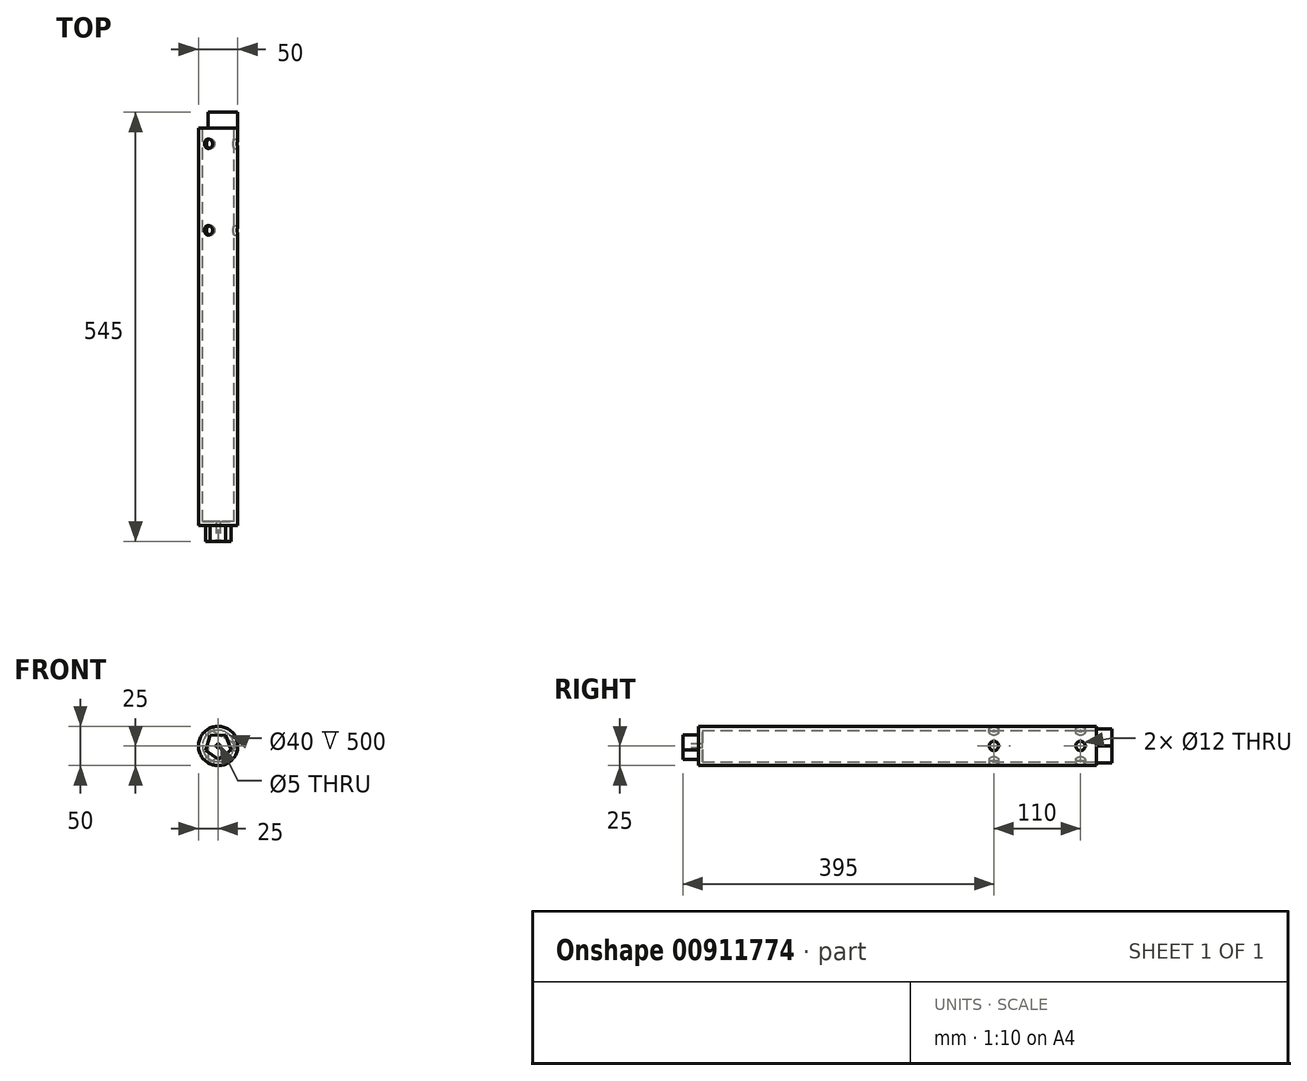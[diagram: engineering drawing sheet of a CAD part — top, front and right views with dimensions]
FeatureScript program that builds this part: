
annotation { "Feature Type Name" : "Feature", "Feature Type Description" : "" }
export const myFeature = defineFeature(function(context is Context, id is Id, definition is map)
    precondition{}
    {
        {
            var Q0;
            Q0=qCreatedBy(makeId("Front.planeOp"),FACE);
            var sketch = newSketch(context, id + "F0", { "sketchPlane" : qUnion([Q0])});
            skCircle(sketch, "E0", {"center": v(0, 0) * mm, "radius": 25 * mm});
            skCircle(sketch, "E1", {"center": v(0, 0) * mm, "radius": 20 * mm});
            skSolve(sketch);
        }
        {
            var Q0;
            Q0=makeQuery(id+"F0.imprint","IMPRINT",FACE,{"disambiguationData":[TD([[makeQuery(id+"F0.imprint","IMPRINT",EDGE,{"derivedFrom":sQuery(id+"F0.wireOp",EDGE,"E0")}),1.0]])]});
            extrude(context, id + "F1", {"entities" : qUnion([Q0]), "depth" : 500 * mm, "offsetDistance" : 25 * mm});
        }
        {
            var Q0;
            Q0=makeQuery(id+"F1.opExtrude","CAP_FACE",FACE,{"disambiguationData":[OSD([sQuery(id+"F0.wireOp",EDGE,"E0"),sQuery(id+"F0.wireOp",EDGE,"E1")])],"isStart":false});
            var sketch = newSketch(context, id + "F2", { "sketchPlane" : qUnion([Q0])});
            skCircle(sketch, "E2", {"center": v(0, 0) * mm, "radius": 25 * mm});
            skSolve(sketch);
        }
        {
            var Q0;
            Q0=qSketchRegion(id+"F2",true);
            extrude(context, id + "F3", {"entities" : qUnion([Q0]), "operationType" : NewBodyOperationType.ADD, "depth" : 5 * mm, "offsetDistance" : 25 * mm});
        }
        {
            var Q0;
            Q0=makeQuery(id+"F3.opExtrude","CAP_FACE",FACE,{"disambiguationData":[OSD([sQuery(id+"F2.wireOp",EDGE,"E2")])],"isStart":false});
            var sketch = newSketch(context, id + "F4", { "sketchPlane" : qUnion([Q0])});
            skCircle(sketch, "E3.cCircle", {"center": v(0, 0) * mm, "radius": 13.77 * mm, "construction": true});
            skLineSegment(sketch, "E3.0", {"start": v(0.38, -17.01) * mm, "end": v(-16.06, -5.62) * mm});
            skLineSegment(sketch, "E3.1", {"start": v(-16.06, -5.62) * mm, "end": v(-10.3, 13.54) * mm});
            skLineSegment(sketch, "E3.2", {"start": v(-10.3, 13.54) * mm, "end": v(9.7, 13.99) * mm});
            skLineSegment(sketch, "E3.3", {"start": v(9.7, 13.99) * mm, "end": v(16.3, -4.9) * mm});
            skLineSegment(sketch, "E3.4", {"start": v(16.3, -4.9) * mm, "end": v(0.38, -17.01) * mm});
            skPoint(sketch, "E3.0.midPoint", {"position": v(-7.84, -11.32) * mm});
            skSolve(sketch);
        }
        {
            var Q0;
            Q0=makeQuery(id+"F4.imprint","IMPRINT",FACE,{"disambiguationData":[TD([[makeQuery(id+"F4.imprint","IMPRINT",EDGE,{"derivedFrom":sQuery(id+"F4.wireOp",EDGE,"E3.0")}),-1.0]])]});
            extrude(context, id + "F5", {"entities" : qUnion([Q0]), "operationType" : NewBodyOperationType.ADD, "depth" : 20 * mm, "offsetDistance" : 25 * mm});
        }
        {
            var Q0;
            Q0=makeQuery(id+"F5.opExtrude","CAP_FACE",FACE,{"disambiguationData":[OSD([sQuery(id+"F4.wireOp",EDGE,"E3.0"),sQuery(id+"F4.wireOp",EDGE,"E3.1"),sQuery(id+"F4.wireOp",EDGE,"E3.2"),sQuery(id+"F4.wireOp",EDGE,"E3.3"),sQuery(id+"F4.wireOp",EDGE,"E3.4")])],"isStart":false});
            var sketch = newSketch(context, id + "F6", { "sketchPlane" : qUnion([Q0])});
            skPoint(sketch, "E4", {"position": v(0, 0) * mm});
            skSolve(sketch);
        }
        {
            var Q0;
            Q0=sQuery(id+"F6.wireOp",VERTEX,"E4");
            var Q1;
            Q1=makeQuery(id+"F1.opExtrude","SWEPT_BODY",BODY,{"disambiguationData":[OSD([sQuery(id+"F0.wireOp",EDGE,"E0"),sQuery(id+"F0.wireOp",EDGE,"E1")])]});
            hole(context, id + "F7", {"style" : HoleStyle.SIMPLE, "endStyle" : HoleEndStyle.THROUGH, "holeDiameter" : 5 * mm, "majorDiameter" : 5 * mm, "isTappedThrough" : true, "tappedDepth" : 12 * mm, "tapClearance" : 3, "locations" : qUnion([Q0]), "scope" : qUnion([Q1])});
        }
        {
            var Q0;
            Q0=qCreatedBy(makeId("Right.planeOp"),FACE);
            cPlane(context, id + "F8", {"entities" : qUnion([Q0]), "cplaneType" : CPlaneType.OFFSET, "offset" : 25 * mm, "width" : 150 * mm, "height" : 150 * mm});
        }
        {
            var Q0;
            Q0=qCreatedBy(id+"F8.planeOp",FACE);
            var sketch = newSketch(context, id + "F9", { "sketchPlane" : qUnion([Q0])});
            skPoint(sketch, "E5", {"position": v(-20, 0) * mm});
            skPoint(sketch, "E6", {"position": v(-130, 0) * mm});
            skSolve(sketch);
        }
        {
            var Q0;
            Q0=sQuery(id+"F9.wireOp",VERTEX,"E5");
            var Q1;
            Q1=sQuery(id+"F9.wireOp",VERTEX,"E6");
            var Q2;
            Q2=makeQuery(id+"F1.opExtrude","SWEPT_BODY",BODY,{"disambiguationData":[OSD([sQuery(id+"F0.wireOp",EDGE,"E0"),sQuery(id+"F0.wireOp",EDGE,"E1")])]});
            hole(context, id + "F10", {"style" : HoleStyle.SIMPLE, "endStyle" : HoleEndStyle.BLIND, "holeDiameter" : 12 * mm, "majorDiameter" : 5 * mm, "holeDepth" : 6 * mm, "isTappedThrough" : true, "tappedDepth" : 12 * mm, "tapClearance" : 3, "locations" : qUnion([Q0, Q1]), "scope" : qUnion([Q2])});
        }
        {
            var Q0;
            Q0=makeQuery(id+"F1.opExtrude","CAP_FACE",FACE,{"disambiguationData":[OSD([sQuery(id+"F0.wireOp",EDGE,"E0"),sQuery(id+"F0.wireOp",EDGE,"E1")])],"isStart":true});
            var sketch = newSketch(context, id + "F11", { "sketchPlane" : qUnion([Q0])});
            skCircle(sketch, "E7.cCircle", {"center": v(0, 0) * mm, "radius": 12.5 * mm, "construction": true});
            skLineSegment(sketch, "E7.0", {"start": v(12.5, 21.65) * mm, "end": v(12.5, -21.65) * mm});
            skLineSegment(sketch, "E7.1", {"start": v(12.5, -21.65) * mm, "end": v(-25, 0) * mm});
            skLineSegment(sketch, "E7.2", {"start": v(-25, 0) * mm, "end": v(12.5, 21.65) * mm});
            skPoint(sketch, "E7.0.midPoint", {"position": v(12.5, 0) * mm});
            skSolve(sketch);
        }
        {
            var Q0;
            Q0=qSketchRegion(id+"F11",true);
            extrude(context, id + "F12", {"entities" : qUnion([Q0]), "operationType" : NewBodyOperationType.ADD, "depth" : 20 * mm, "offsetDistance" : 25 * mm});
        }
        {
            var Q0;
            Q0=qCreatedBy(makeId("Front.planeOp"),FACE);
            cPlane(context, id + "F13", {"entities" : qUnion([Q0]), "cplaneType" : CPlaneType.OFFSET, "offset" : 25 * mm, "width" : 150 * mm, "height" : 150 * mm});
        }
        {
            var Q0;
            Q0=makeQuery(id+"F12.opExtrude","SWEPT_FACE",FACE,{"disambiguationData":[OSD([sQuery(id+"F11.wireOp",EDGE,"E7.2")])]});
            cPlane(context, id + "F14", {"entities" : qUnion([Q0]), "cplaneType" : CPlaneType.OFFSET, "offset" : 37.5 * mm, "oppositeDirection" : true, "width" : 150 * mm, "height" : 150 * mm});
        }
        {
            var Q0;
            Q0=makeQuery(id+"F12.opExtrude","SWEPT_FACE",FACE,{"disambiguationData":[OSD([sQuery(id+"F11.wireOp",EDGE,"E7.1")])]});
            cPlane(context, id + "F15", {"entities" : qUnion([Q0]), "cplaneType" : CPlaneType.OFFSET, "offset" : 37.5 * mm, "oppositeDirection" : true, "width" : 150 * mm, "height" : 150 * mm});
        }
        {
            var Q0;
            Q0=qCreatedBy(id+"F14.planeOp",FACE);
            var sketch = newSketch(context, id + "F16", { "sketchPlane" : qUnion([Q0])});
            skLineSegment(sketch, "E8", {"start": v(0, 0) * mm, "end": v(0, -597.57) * mm});
            skPoint(sketch, "E9", {"position": v(0, -20) * mm});
            skPoint(sketch, "E10", {"position": v(0, -130) * mm});
            skSolve(sketch);
        }
        {
            var Q0;
            Q0=sQuery(id+"F16.wireOp",VERTEX,"E9");
            var Q1;
            Q1=sQuery(id+"F16.wireOp",VERTEX,"E10");
            var Q2;
            Q2=makeQuery(id+"F1.opExtrude","SWEPT_BODY",BODY,{"disambiguationData":[OSD([sQuery(id+"F0.wireOp",EDGE,"E0"),sQuery(id+"F0.wireOp",EDGE,"E1")])]});
            hole(context, id + "F17", {"style" : HoleStyle.SIMPLE, "endStyle" : HoleEndStyle.BLIND, "oppositeDirection" : true, "holeDiameter" : 12 * mm, "majorDiameter" : 5 * mm, "holeDepth" : 6 * mm, "isTappedThrough" : true, "tappedDepth" : 12 * mm, "tapClearance" : 3, "locations" : qUnion([Q0, Q1]), "scope" : qUnion([Q2])});
        }
        {
            var Q0;
            Q0=qCreatedBy(id+"F15.planeOp",FACE);
            var sketch = newSketch(context, id + "F18", { "sketchPlane" : qUnion([Q0])});
            skLineSegment(sketch, "E11", {"start": v(0, 0) * mm, "end": v(0, 1140.88) * mm});
            skPoint(sketch, "E12", {"position": v(0, 20) * mm});
            skPoint(sketch, "E13", {"position": v(0, 130) * mm});
            skSolve(sketch);
        }
        {
            var Q0;
            Q0=sQuery(id+"F18.wireOp",VERTEX,"E12");
            var Q1;
            Q1=sQuery(id+"F18.wireOp",VERTEX,"E13");
            var Q2;
            Q2=makeQuery(id+"F1.opExtrude","SWEPT_BODY",BODY,{"disambiguationData":[OSD([sQuery(id+"F0.wireOp",EDGE,"E0"),sQuery(id+"F0.wireOp",EDGE,"E1")])]});
            hole(context, id + "F19", {"style" : HoleStyle.SIMPLE, "endStyle" : HoleEndStyle.BLIND, "oppositeDirection" : true, "holeDiameter" : 12 * mm, "majorDiameter" : 5 * mm, "holeDepth" : 6 * mm, "isTappedThrough" : true, "tappedDepth" : 12 * mm, "tapClearance" : 3, "locations" : qUnion([Q0, Q1]), "scope" : qUnion([Q2])});
        }
    });
